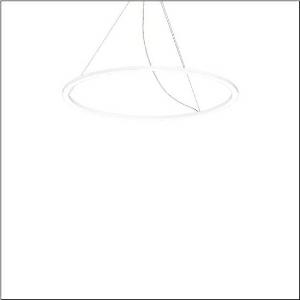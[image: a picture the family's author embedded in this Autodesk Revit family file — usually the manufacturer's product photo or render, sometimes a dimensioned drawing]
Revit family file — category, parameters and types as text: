
# Revit family: silica_21_ring-d_5pjbd3d3004a
name_source: partatom
category: Lighting Fixtures
units: mm (PartAtom-declared; Revit-internal decimal feet)

## family parameters
Cut with Voids When Loaded = No
Host = Face
Light Source = No
Part Type = Normal
Room Calculation Point = No
Round Connector Dimension = Use Diameter
Shared = No

## types (1)
- Silica 21 Ring-D (1 x LED, 8420 lm, 94 W, 4000K)
    Apparent Load = 94 VA
    CIE Flux Codes = 37 69 92 100 100
    Color Rendering = 80
    Color Temperature = 4000K
    Default Elevation = 1800 mm
    Description = Silica 21 Ring-D, suspended luminaire, of PMMA, frosted, light emission: ring underside luminous distribution, primary light characteristic: symmetric, installation type: suspended mounting, LED, rated luminous flux: 8.420lm, luminous efficacy: 90lm/W, light colour: 840, colour temperature: 4000K, control gear: DALI 2, with terminal, 5-pole, mains connection: 230V, AC/DC, 0/50..60Hz, rated input power: 94W, housing, of extruded aluminium section, traffic white (RAL 9016), diameter: 1.100mm, ceiling canopy, traffic white (RAL 9016), protection rating (lamp compartment): IP40, insulation class (complete): insulation class I (protective earthing), certification: CE, impact resistance: IK02, permissible operating ambient temperature: 0..+35°C, packaging unit: 1 piece
    Height = 25 mm  [stored 0.082021 ft]
    Lamp = 1 x LED
    Lamp Light Flux = 8420 lm
    Lamp Power = 94 W
    Lamp count = 1
    Length = 1100 mm
    Luminous efficacy = 90 lm/W
    Manufacturer = Siteco
    ModVariant = No
    Model = 5PJBD3D3004A
    Mounting Place = Ceiling
    Mounting Type = Pendant
    Number of Poles = 1
    OnlyDefault = Yes
    Power Factor = 1
    Product Name = Silica 21 Ring-D
    Product group = suspended luminaire
    ProductGroupID = 904
    Protection Class = Protection class I
    Protection Degree = IP 40
    RLX_Detail_Level = 1
    RLX_Emergency_Light_Flux = 0 lm
    RLX_Emergency_Type = 0
    RLX_Emergency_Type_DB = No
    RlxData = <blob elided: 12497 chars, md5=b90ae608>
    Socket = socket
    Standby Power = 0 W
    System Light Flux = 8420 lm
    System Power = 94 W
    Type Comments = Product without accessories
    Type Image = l_1258355.jpg
    URL = http://relux.com
    VarID = ---
    Voltage = 0 V
    Weight = 0.00 kg
    Width = 0 mm  [stored 0 ft]

note: [stored X ft] marks values corroborated as IEEE doubles in the binary element streams (Revit-internal decimal feet)

## geometry (parser evidence)
native form markers: Sweep x9
no freeform markers — native parametric forms only
